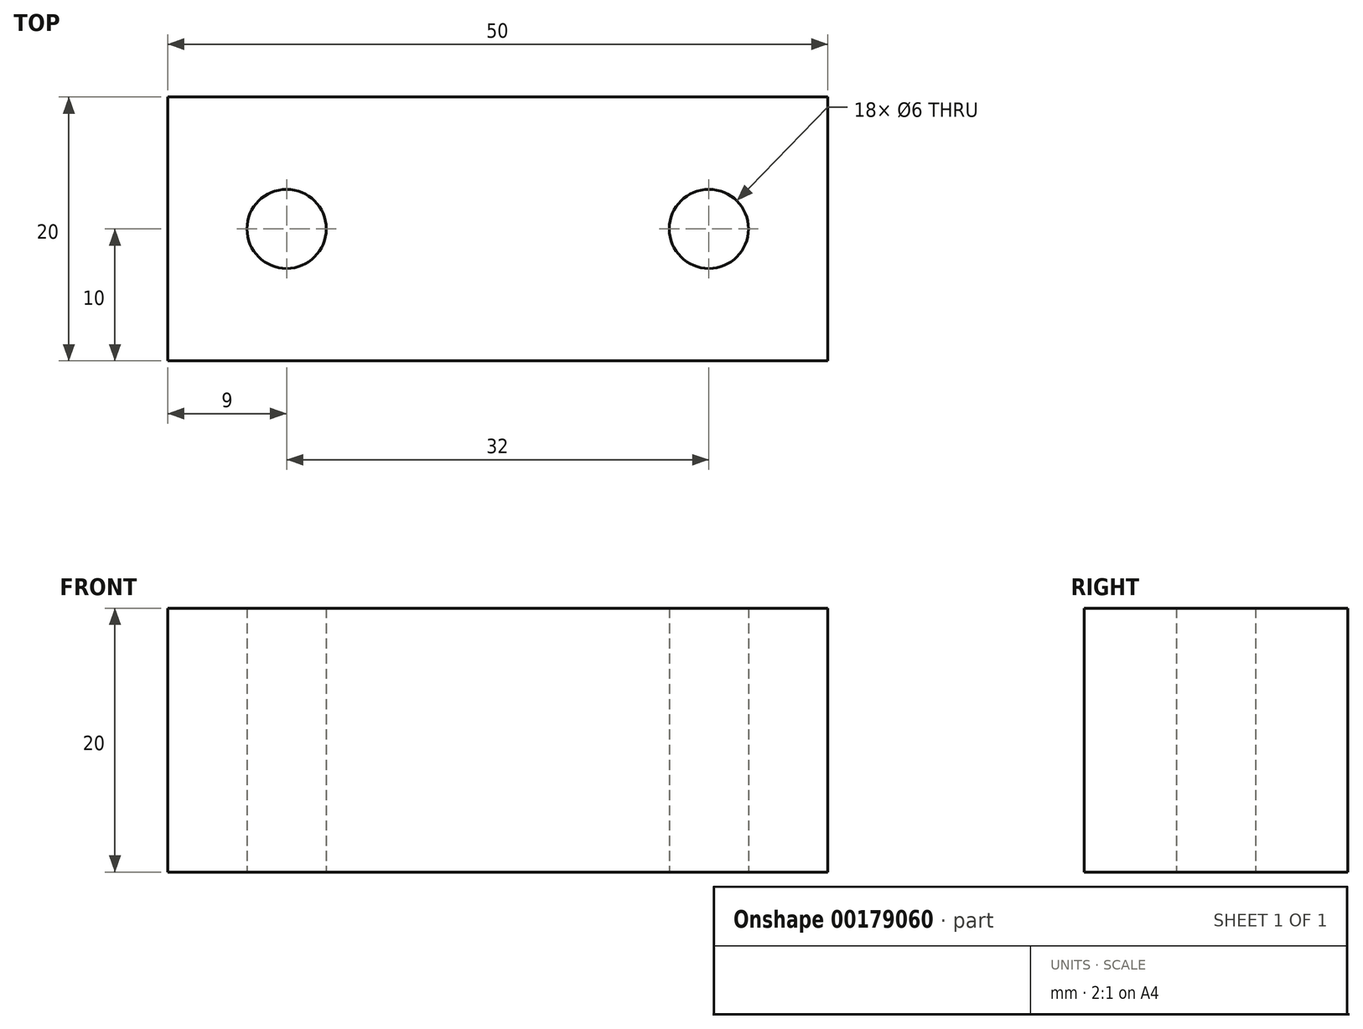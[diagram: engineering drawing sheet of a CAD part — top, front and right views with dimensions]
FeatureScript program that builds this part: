
annotation { "Feature Type Name" : "Feature", "Feature Type Description" : "" }
export const myFeature = defineFeature(function(context is Context, id is Id, definition is map)
    precondition{}
    {
        {
            var Q0;
            Q0=qCreatedBy(makeId("Top.planeOp"),FACE);
            var sketch = newSketch(context, id + "F0", { "sketchPlane" : qUnion([Q0])});
            skLineSegment(sketch, "E0.bottom", {"start": v(25, -10) * mm, "end": v(-25, -10) * mm});
            skLineSegment(sketch, "E0.top", {"start": v(25, 10) * mm, "end": v(-25, 10) * mm});
            skLineSegment(sketch, "E0.left", {"start": v(25, -10) * mm, "end": v(25, 10) * mm});
            skLineSegment(sketch, "E0.right", {"start": v(-25, -10) * mm, "end": v(-25, 10) * mm});
            skPoint(sketch, "E0.middle", {"position": v(0, 0) * mm});
            skLineSegment(sketch, "E1", {"start": v(-20.17, 0) * mm, "end": v(26.64, 0) * mm, "construction": true});
            skCircle(sketch, "E2", {"center": v(-16, 0) * mm, "radius": 3 * mm});
            skCircle(sketch, "E3", {"center": v(16, 0) * mm, "radius": 3 * mm});
            skSolve(sketch);
        }
        {
            var Q0;
            Q0 = qSketchRegion(id + "F0", true);
            extrude(context, id + "F1", {"entities" : qUnion([Q0]), "depth" : 20 * mm});
        }
    });
